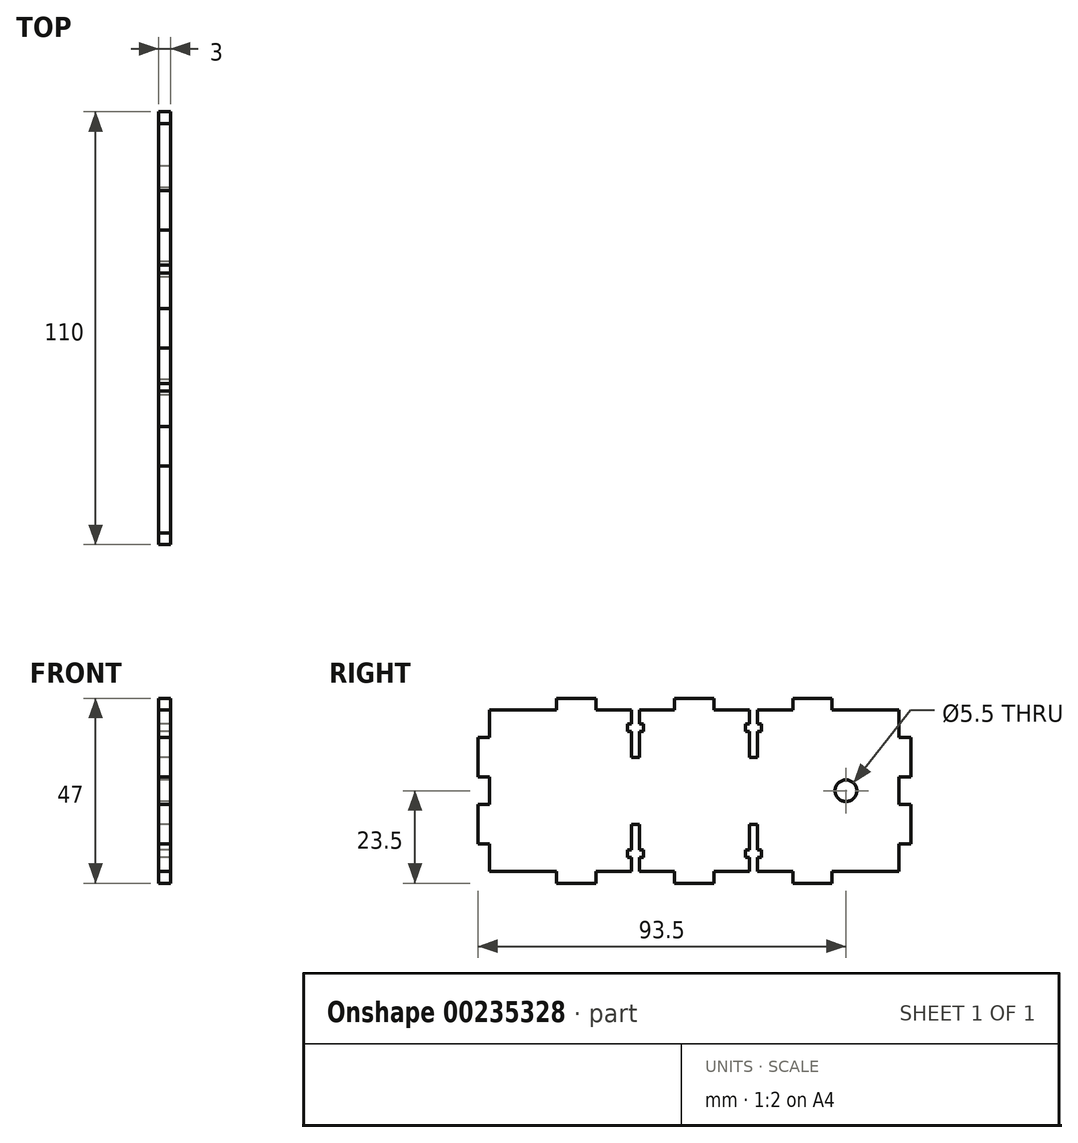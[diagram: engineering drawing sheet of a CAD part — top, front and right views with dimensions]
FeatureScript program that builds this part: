
annotation { "Feature Type Name" : "Feature", "Feature Type Description" : "" }
export const myFeature = defineFeature(function(context is Context, id is Id, definition is map)
    precondition{}
    {
        {
            var Q0;
            Q0=qCreatedBy(makeId("Right.planeOp"),FACE);
            var sketch = newSketch(context, id + "F0", { "sketchPlane" : qUnion([Q0])});
            skLineSegment(sketch, "E0", {"start": v(0, 0) * mm, "end": v(0, 7) * mm});
            skLineSegment(sketch, "E1", {"start": v(0, 7) * mm, "end": v(-3, 7) * mm});
            skLineSegment(sketch, "E2", {"start": v(-3, 7) * mm, "end": v(-3, 17) * mm});
            skLineSegment(sketch, "E3", {"start": v(-3, 17) * mm, "end": v(0, 17) * mm});
            skLineSegment(sketch, "E4", {"start": v(0, 17) * mm, "end": v(0, 24) * mm});
            skLineSegment(sketch, "E5", {"start": v(0, 24) * mm, "end": v(-3, 24) * mm});
            skLineSegment(sketch, "E6", {"start": v(-3, 24) * mm, "end": v(-3, 34) * mm});
            skLineSegment(sketch, "E7", {"start": v(-3, 34) * mm, "end": v(0, 34) * mm});
            skLineSegment(sketch, "E8", {"start": v(0, 34) * mm, "end": v(0, 41) * mm});
            skLineSegment(sketch, "E9", {"start": v(0, 41) * mm, "end": v(17, 41) * mm});
            skLineSegment(sketch, "E10", {"start": v(17, 41) * mm, "end": v(17, 44) * mm});
            skLineSegment(sketch, "E11", {"start": v(17, 44) * mm, "end": v(27, 44) * mm});
            skLineSegment(sketch, "E12", {"start": v(27, 44) * mm, "end": v(27, 41) * mm});
            skLineSegment(sketch, "E13", {"start": v(27, 41) * mm, "end": v(36, 41) * mm});
            skLineSegment(sketch, "E14", {"start": v(47, 41) * mm, "end": v(47, 44) * mm});
            skLineSegment(sketch, "E15", {"start": v(47, 44) * mm, "end": v(52, 44) * mm});
            skLineSegment(sketch, "E16.MirrorCS", {"start": v(47, 0) * mm, "end": v(47, -3) * mm});
            skLineSegment(sketch, "E17.MirrorCS", {"start": v(27, -3) * mm, "end": v(27, 0) * mm});
            skLineSegment(sketch, "E18.MirrorCS", {"start": v(17, 0) * mm, "end": v(17, -3) * mm});
            skLineSegment(sketch, "E19.MirrorCS", {"start": v(47, -3) * mm, "end": v(52, -3) * mm});
            skLineSegment(sketch, "E20.MirrorCS", {"start": v(27, 0) * mm, "end": v(33.54, 0) * mm});
            skLineSegment(sketch, "E21.MirrorCS", {"start": v(0, 0) * mm, "end": v(17, 0) * mm});
            skLineSegment(sketch, "E22.MirrorCS", {"start": v(17, -3) * mm, "end": v(27, -3) * mm});
            skLineSegment(sketch, "E23.MirrorCS", {"start": v(57, -3) * mm, "end": v(52, -3) * mm});
            skLineSegment(sketch, "E24.MirrorCS", {"start": v(57, 44) * mm, "end": v(52, 44) * mm});
            skLineSegment(sketch, "E25.top", {"start": v(36, 29) * mm, "end": v(38, 29) * mm});
            skLineSegment(sketch, "E25.left", {"start": v(36, 41) * mm, "end": v(36, 37.5) * mm});
            skLineSegment(sketch, "E25.right", {"start": v(38, 41) * mm, "end": v(38, 37.5) * mm});
            skLineSegment(sketch, "E26.MirrorCS", {"start": v(33.54, 41) * mm, "end": v(36, 41) * mm});
            skPoint(sketch, "E27.endSnap0", {"position": v(37, 29) * mm});
            skLineSegment(sketch, "E28.bottom", {"start": v(35, 37.5) * mm, "end": v(36, 37.5) * mm});
            skLineSegment(sketch, "E28.top", {"start": v(35, 35.5) * mm, "end": v(36, 35.5) * mm});
            skLineSegment(sketch, "E28.left", {"start": v(35, 37.5) * mm, "end": v(35, 35.5) * mm});
            skLineSegment(sketch, "E28.right", {"start": v(39, 37.5) * mm, "end": v(39, 35.5) * mm});
            skLineSegment(sketch, "E29.trimOffspring", {"start": v(38, 41) * mm, "end": v(47, 41) * mm});
            skLineSegment(sketch, "E30.trimOffspring", {"start": v(38, 41) * mm, "end": v(38.1, 41) * mm});
            skLineSegment(sketch, "E31.trimOffspring", {"start": v(38, 37.5) * mm, "end": v(39, 37.5) * mm});
            skLineSegment(sketch, "E32.trimOffspring", {"start": v(36, 35.5) * mm, "end": v(36, 29) * mm});
            skLineSegment(sketch, "E33.trimOffspring", {"start": v(38, 35.5) * mm, "end": v(38, 29) * mm});
            skLineSegment(sketch, "E34.trimOffspring", {"start": v(38, 35.5) * mm, "end": v(39, 35.5) * mm});
            skLineSegment(sketch, "E35.MirrorCS", {"start": v(38, 0) * mm, "end": v(38.1, 0) * mm});
            skLineSegment(sketch, "E36.MirrorCS", {"start": v(35, 3.5) * mm, "end": v(36, 3.5) * mm});
            skLineSegment(sketch, "E37.MirrorCS", {"start": v(38, 5.5) * mm, "end": v(39, 5.5) * mm});
            skLineSegment(sketch, "E38.MirrorCS", {"start": v(35, 5.5) * mm, "end": v(36, 5.5) * mm});
            skLineSegment(sketch, "E39.MirrorCS", {"start": v(38, 3.5) * mm, "end": v(39, 3.5) * mm});
            skLineSegment(sketch, "E40.MirrorCS", {"start": v(36, 12) * mm, "end": v(38, 12) * mm});
            skLineSegment(sketch, "E41.MirrorCS", {"start": v(36, 5.5) * mm, "end": v(36, 12) * mm});
            skLineSegment(sketch, "E42.MirrorCS", {"start": v(38, 5.5) * mm, "end": v(38, 12) * mm});
            skLineSegment(sketch, "E43.MirrorCS", {"start": v(35, 3.5) * mm, "end": v(35, 5.5) * mm});
            skLineSegment(sketch, "E44.MirrorCS", {"start": v(36, 0) * mm, "end": v(36, 3.5) * mm});
            skLineSegment(sketch, "E45.MirrorCS", {"start": v(39, 3.5) * mm, "end": v(39, 5.5) * mm});
            skLineSegment(sketch, "E46.MirrorCS", {"start": v(38, 0) * mm, "end": v(38, 3.5) * mm});
            skPoint(sketch, "E47.MirrorP", {"position": v(37, 12) * mm});
            skLineSegment(sketch, "E48.MirrorCS", {"start": v(33.54, 0) * mm, "end": v(36, 0) * mm});
            skLineSegment(sketch, "E49.trimOffspring", {"start": v(38, 0) * mm, "end": v(47, 0) * mm});
            skLineSegment(sketch, "E50", {"start": v(52, 44) * mm, "end": v(52, -3) * mm, "construction": true});
            skLineSegment(sketch, "E51.MirrorCS", {"start": v(66, 41) * mm, "end": v(65.9, 41) * mm});
            skLineSegment(sketch, "E52.MirrorCS", {"start": v(66, 0) * mm, "end": v(65.9, 0) * mm});
            skLineSegment(sketch, "E53.MirrorCS", {"start": v(69, 3.5) * mm, "end": v(68, 3.5) * mm});
            skLineSegment(sketch, "E54.MirrorCS", {"start": v(66, 5.5) * mm, "end": v(65, 5.5) * mm});
            skLineSegment(sketch, "E55.MirrorCS", {"start": v(66, 3.5) * mm, "end": v(65, 3.5) * mm});
            skLineSegment(sketch, "E56.MirrorCS", {"start": v(69, 5.5) * mm, "end": v(68, 5.5) * mm});
            skLineSegment(sketch, "E57.MirrorCS", {"start": v(69, 35.5) * mm, "end": v(68, 35.5) * mm});
            skLineSegment(sketch, "E58.MirrorCS", {"start": v(66, 37.5) * mm, "end": v(65, 37.5) * mm});
            skLineSegment(sketch, "E59.MirrorCS", {"start": v(66, 35.5) * mm, "end": v(65, 35.5) * mm});
            skLineSegment(sketch, "E60.MirrorCS", {"start": v(69, 37.5) * mm, "end": v(68, 37.5) * mm});
            skLineSegment(sketch, "E61.MirrorCS", {"start": v(68, 29) * mm, "end": v(66, 29) * mm});
            skLineSegment(sketch, "E62.MirrorCS", {"start": v(107, 17) * mm, "end": v(104, 17) * mm});
            skLineSegment(sketch, "E63.MirrorCS", {"start": v(68, 12) * mm, "end": v(66, 12) * mm});
            skLineSegment(sketch, "E64.MirrorCS", {"start": v(70.46, 41) * mm, "end": v(68, 41) * mm});
            skLineSegment(sketch, "E65.MirrorCS", {"start": v(65, 3.5) * mm, "end": v(65, 5.5) * mm});
            skLineSegment(sketch, "E66.MirrorCS", {"start": v(66, 41) * mm, "end": v(57, 41) * mm});
            skLineSegment(sketch, "E67.MirrorCS", {"start": v(77, 0) * mm, "end": v(70.46, 0) * mm});
            skLineSegment(sketch, "E68.MirrorCS", {"start": v(107, 7) * mm, "end": v(107, 17) * mm});
            skLineSegment(sketch, "E69.MirrorCS", {"start": v(104, 17) * mm, "end": v(104, 24) * mm});
            skLineSegment(sketch, "E70.MirrorCS", {"start": v(104, 24) * mm, "end": v(107, 24) * mm});
            skLineSegment(sketch, "E71.MirrorCS", {"start": v(66, 0) * mm, "end": v(66, 3.5) * mm});
            skLineSegment(sketch, "E72.MirrorCS", {"start": v(66, 41) * mm, "end": v(66, 37.5) * mm});
            skLineSegment(sketch, "E73.MirrorCS", {"start": v(107, 24) * mm, "end": v(107, 34) * mm});
            skLineSegment(sketch, "E74.MirrorCS", {"start": v(104, 34) * mm, "end": v(104, 41) * mm});
            skLineSegment(sketch, "E75.MirrorCS", {"start": v(107, 34) * mm, "end": v(104, 34) * mm});
            skLineSegment(sketch, "E76.MirrorCS", {"start": v(87, 41) * mm, "end": v(87, 44) * mm});
            skLineSegment(sketch, "E77.MirrorCS", {"start": v(104, 41) * mm, "end": v(87, 41) * mm});
            skLineSegment(sketch, "E78.MirrorCS", {"start": v(87, 44) * mm, "end": v(77, 44) * mm});
            skLineSegment(sketch, "E79.MirrorCS", {"start": v(77, 44) * mm, "end": v(77, 41) * mm});
            skLineSegment(sketch, "E80.MirrorCS", {"start": v(66, 35.5) * mm, "end": v(66, 29) * mm});
            skLineSegment(sketch, "E81.MirrorCS", {"start": v(68, 41) * mm, "end": v(68, 37.5) * mm});
            skPoint(sketch, "E82.MirrorP", {"position": v(67, 29) * mm});
            skLineSegment(sketch, "E83.MirrorCS", {"start": v(57, 0) * mm, "end": v(57, -3) * mm});
            skLineSegment(sketch, "E84.MirrorCS", {"start": v(66, 5.5) * mm, "end": v(66, 12) * mm});
            skLineSegment(sketch, "E85.MirrorCS", {"start": v(104, 0) * mm, "end": v(87, 0) * mm});
            skPoint(sketch, "E86.MirrorP", {"position": v(67, 12) * mm});
            skLineSegment(sketch, "E87.MirrorCS", {"start": v(70.46, 0) * mm, "end": v(68, 0) * mm});
            skLineSegment(sketch, "E88.MirrorCS", {"start": v(77, -3) * mm, "end": v(77, 0) * mm});
            skLineSegment(sketch, "E89.MirrorCS", {"start": v(69, 3.5) * mm, "end": v(69, 5.5) * mm});
            skLineSegment(sketch, "E90.MirrorCS", {"start": v(69, 37.5) * mm, "end": v(69, 35.5) * mm});
            skLineSegment(sketch, "E91.MirrorCS", {"start": v(87, 0) * mm, "end": v(87, -3) * mm});
            skLineSegment(sketch, "E92.MirrorCS", {"start": v(65, 37.5) * mm, "end": v(65, 35.5) * mm});
            skLineSegment(sketch, "E93.MirrorCS", {"start": v(68, 0) * mm, "end": v(68, 3.5) * mm});
            skLineSegment(sketch, "E94.MirrorCS", {"start": v(87, -3) * mm, "end": v(77, -3) * mm});
            skLineSegment(sketch, "E95.MirrorCS", {"start": v(68, 5.5) * mm, "end": v(68, 12) * mm});
            skLineSegment(sketch, "E96.MirrorCS", {"start": v(66, 0) * mm, "end": v(57, 0) * mm});
            skLineSegment(sketch, "E97.MirrorCS", {"start": v(68, 35.5) * mm, "end": v(68, 29) * mm});
            skLineSegment(sketch, "E98.MirrorCS", {"start": v(77, 41) * mm, "end": v(68, 41) * mm});
            skLineSegment(sketch, "E99.MirrorCS", {"start": v(57, 41) * mm, "end": v(57, 44) * mm});
            skLineSegment(sketch, "E100.MirrorCS", {"start": v(104, 0) * mm, "end": v(104, 7) * mm});
            skLineSegment(sketch, "E101.MirrorCS", {"start": v(104, 7) * mm, "end": v(107, 7) * mm});
            skCircle(sketch, "E102", {"center": v(90.5, 20.5) * mm, "radius": 2.75 * mm});
            skSolve(sketch);
        }
        {
            var Q0;
            Q0 = qSketchRegion(id + "F0", true);
            extrude(context, id + "F1", {"entities" : qUnion([Q0]), "depth" : 3 * mm});
        }
    });
